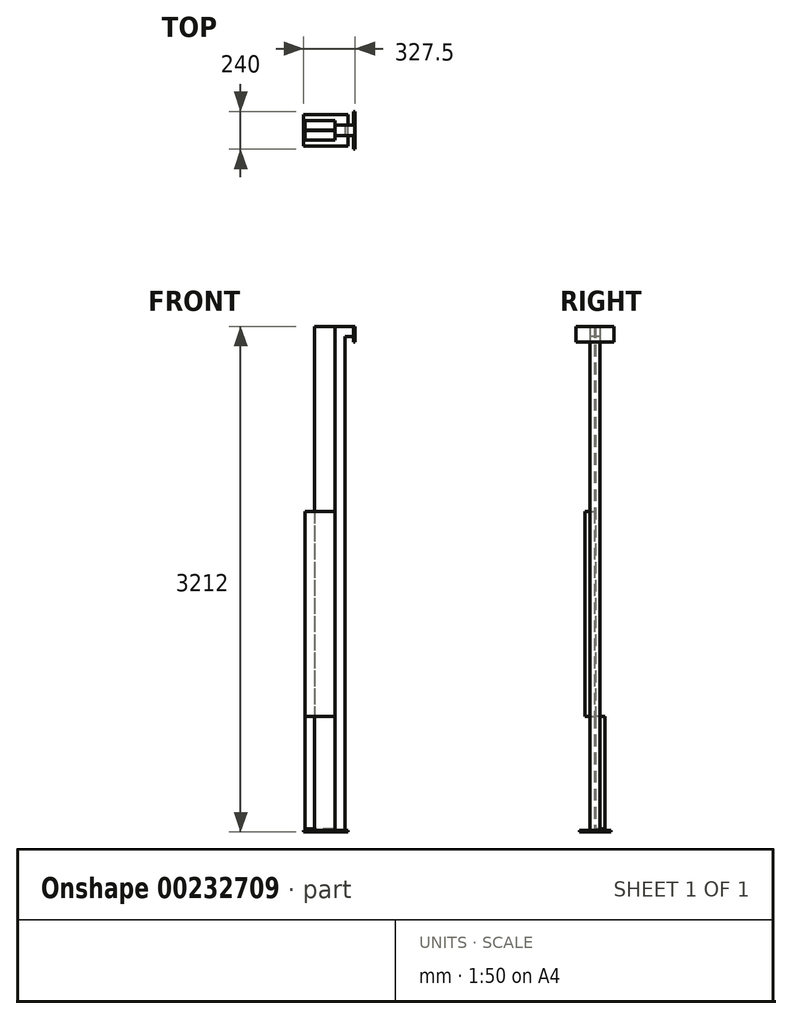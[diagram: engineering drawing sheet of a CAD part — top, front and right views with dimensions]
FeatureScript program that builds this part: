
annotation { "Feature Type Name" : "Feature", "Feature Type Description" : "" }
export const myFeature = defineFeature(function(context is Context, id is Id, definition is map)
    precondition{}
    {
        {
            var Q0;
            Q0=qCreatedBy(makeId("Top.planeOp"),FACE);
            var sketch = newSketch(context, id + "F0", { "sketchPlane" : qUnion([Q0])});
            skLineSegment(sketch, "E0.bottom", {"start": v(0, 0) * mm, "end": v(-280, 0) * mm});
            skLineSegment(sketch, "E0.top", {"start": v(0, 200) * mm, "end": v(-280, 200) * mm});
            skLineSegment(sketch, "E0.left", {"start": v(0, 0) * mm, "end": v(0, 200) * mm});
            skLineSegment(sketch, "E0.right", {"start": v(-280, 0) * mm, "end": v(-280, 200) * mm});
            skSolve(sketch);
        }
        {
            var Q0;
            Q0 = qSketchRegion(id + "F0", true);
            extrude(context, id + "F1", {"entities" : qUnion([Q0]), "depth" : 12 * mm});
        }
        {
            var Q0;
            Q0=makeQuery(id+"F1.opExtrude","CAP_FACE",FACE,{"disambiguationData":[OSD([sQuery(id+"F0.wireOp",EDGE,"E0.bottom"),sQuery(id+"F0.wireOp",EDGE,"E0.top"),sQuery(id+"F0.wireOp",EDGE,"E0.left"),sQuery(id+"F0.wireOp",EDGE,"E0.right")])],"isStart":false});
            var sketch = newSketch(context, id + "F2", { "sketchPlane" : qUnion([Q0])});
            skLineSegment(sketch, "E1.bottom", {"start": v(-82.5, 132.5) * mm, "end": v(-17.5, 132.5) * mm});
            skLineSegment(sketch, "E1.top", {"start": v(-82.5, 67.5) * mm, "end": v(-17.5, 67.5) * mm});
            skLineSegment(sketch, "E1.left", {"start": v(-82.5, 132.5) * mm, "end": v(-82.5, 67.5) * mm});
            skLineSegment(sketch, "E1.right", {"start": v(-17.5, 132.5) * mm, "end": v(-17.5, 67.5) * mm});
            skLineSegment(sketch, "E2", {"start": v(-50, 132.5) * mm, "end": v(-50, 67.5) * mm, "construction": true});
            skLineSegment(sketch, "E3", {"start": v(-82.5, 100) * mm, "end": v(-17.5, 100) * mm, "construction": true});
            skSolve(sketch);
        }
        {
            var Q0;
            Q0 = qSketchRegion(id + "F2", true);
            extrude(context, id + "F3", {"entities" : qUnion([Q0]), "operationType" : NewBodyOperationType.ADD, "depth" : 3200 * mm});
        }
        {
            var Q0;
            Q0=makeQuery(id+"F3.opExtrude","SWEPT_FACE",FACE,{"disambiguationData":[OSD([sQuery(id+"F2.wireOp",EDGE,"E1.right")])]});
            var sketch = newSketch(context, id + "F4", { "sketchPlane" : qUnion([Q0])});
            skLineSegment(sketch, "E4.bottom", {"start": v(132.5, 3212) * mm, "end": v(67.5, 3212) * mm});
            skLineSegment(sketch, "E4.top", {"start": v(132.5, 3147) * mm, "end": v(67.5, 3147) * mm});
            skLineSegment(sketch, "E4.left", {"start": v(132.5, 3212) * mm, "end": v(132.5, 3147) * mm});
            skLineSegment(sketch, "E4.right", {"start": v(67.5, 3212) * mm, "end": v(67.5, 3147) * mm});
            skSolve(sketch);
        }
        {
            var Q0;
            Q0 = qSketchRegion(id + "F4", true);
            extrude(context, id + "F5", {"entities" : qUnion([Q0]), "operationType" : NewBodyOperationType.ADD, "depth" : (65 - 12) * mm});
        }
        {
            var Q0;
            Q0=makeQuery(id+"F5.opExtrude","CAP_FACE",FACE,{"disambiguationData":[OSD([sQuery(id+"F4.wireOp",EDGE,"E4.bottom"),sQuery(id+"F4.wireOp",EDGE,"E4.top"),sQuery(id+"F4.wireOp",EDGE,"E4.left"),sQuery(id+"F4.wireOp",EDGE,"E4.right")])],"isStart":false});
            var sketch = newSketch(context, id + "F6", { "sketchPlane" : qUnion([Q0])});
            skLineSegment(sketch, "E5.bottom", {"start": v(220, 3212) * mm, "end": v(-20, 3212) * mm});
            skLineSegment(sketch, "E5.top", {"start": v(220, 3112) * mm, "end": v(-20, 3112) * mm});
            skLineSegment(sketch, "E5.left", {"start": v(220, 3212) * mm, "end": v(220, 3112) * mm});
            skLineSegment(sketch, "E5.right", {"start": v(-20, 3212) * mm, "end": v(-20, 3112) * mm});
            skPoint(sketch, "E6.endSnap0", {"position": v(100, 3147) * mm});
            skLineSegment(sketch, "E7", {"start": v(100, 3212) * mm, "end": v(100, 3112) * mm, "construction": true});
            skLineSegment(sketch, "E8", {"start": v(100, 3212) * mm, "end": v(100, 3147) * mm, "construction": true});
            skSolve(sketch);
        }
        {
            var Q0;
            Q0 = qSketchRegion(id + "F6", true);
            extrude(context, id + "F7", {"entities" : qUnion([Q0]), "operationType" : NewBodyOperationType.ADD, "depth" : 12 * mm});
        }
        {
            var Q0;
            Q0=makeQuery(id+"F1.opExtrude","CAP_FACE",FACE,{"disambiguationData":[OSD([sQuery(id+"F0.wireOp",EDGE,"E0.bottom"),sQuery(id+"F0.wireOp",EDGE,"E0.top"),sQuery(id+"F0.wireOp",EDGE,"E0.left"),sQuery(id+"F0.wireOp",EDGE,"E0.right")])],"isStart":false});
            var sketch = newSketch(context, id + "F8", { "sketchPlane" : qUnion([Q0])});
            skLineSegment(sketch, "E9.bottom", {"start": v(-82.5, 102.5) * mm, "end": v(-212.5, 102.5) * mm});
            skLineSegment(sketch, "E9.top", {"start": v(-82.5, 97.5) * mm, "end": v(-212.5, 97.5) * mm});
            skLineSegment(sketch, "E9.left", {"start": v(-82.5, 102.5) * mm, "end": v(-82.5, 97.5) * mm});
            skLineSegment(sketch, "E9.right", {"start": v(-212.5, 102.5) * mm, "end": v(-212.5, 97.5) * mm});
            skSolve(sketch);
        }
        {
            var Q0;
            Q0 = qSketchRegion(id + "F8", true);
            extrude(context, id + "F9", {"entities" : qUnion([Q0]), "operationType" : NewBodyOperationType.ADD, "depth" : 3200 * mm});
        }
        {
            var Q0;
            Q0=makeQuery(id+"F9.opExtrude","SWEPT_FACE",FACE,{"disambiguationData":[OSD([sQuery(id+"F8.wireOp",EDGE,"E9.bottom")])]});
            var sketch = newSketch(context, id + "F10", { "sketchPlane" : qUnion([Q0])});
            skLineSegment(sketch, "E10.bottom", {"start": v(82.5, 20) * mm, "end": v(272.5, 20) * mm});
            skLineSegment(sketch, "E10.top", {"start": v(82.5, 735) * mm, "end": v(272.5, 735) * mm});
            skLineSegment(sketch, "E10.left", {"start": v(82.5, 20) * mm, "end": v(82.5, 735) * mm});
            skLineSegment(sketch, "E10.right", {"start": v(272.5, 20) * mm, "end": v(272.5, 735) * mm});
            skSolve(sketch);
        }
        {
            var Q0;
            Q0 = qSketchRegion(id + "F10", true);
            extrude(context, id + "F11", {"entities" : qUnion([Q0]), "operationType" : NewBodyOperationType.ADD, "depth" : 60 * mm});
        }
        {
            var Q0;
            Q0=makeQuery(id+"F9.opExtrude","SWEPT_FACE",FACE,{"disambiguationData":[OSD([sQuery(id+"F8.wireOp",EDGE,"E9.top")])]});
            var sketch = newSketch(context, id + "F12", { "sketchPlane" : qUnion([Q0])});
            skLineSegment(sketch, "E11.bottom", {"start": v(-82.5, 2035) * mm, "end": v(-272.5, 2035) * mm});
            skLineSegment(sketch, "E11.top", {"start": v(-82.5, 735) * mm, "end": v(-272.5, 735) * mm});
            skLineSegment(sketch, "E11.left", {"start": v(-82.5, 2035) * mm, "end": v(-82.5, 735) * mm});
            skLineSegment(sketch, "E11.right", {"start": v(-272.5, 2035) * mm, "end": v(-272.5, 735) * mm});
            skSolve(sketch);
        }
        {
            var Q0;
            Q0 = qSketchRegion(id + "F12", true);
            extrude(context, id + "F13", {"entities" : qUnion([Q0]), "operationType" : NewBodyOperationType.ADD, "depth" : 60 * mm});
        }
    });
